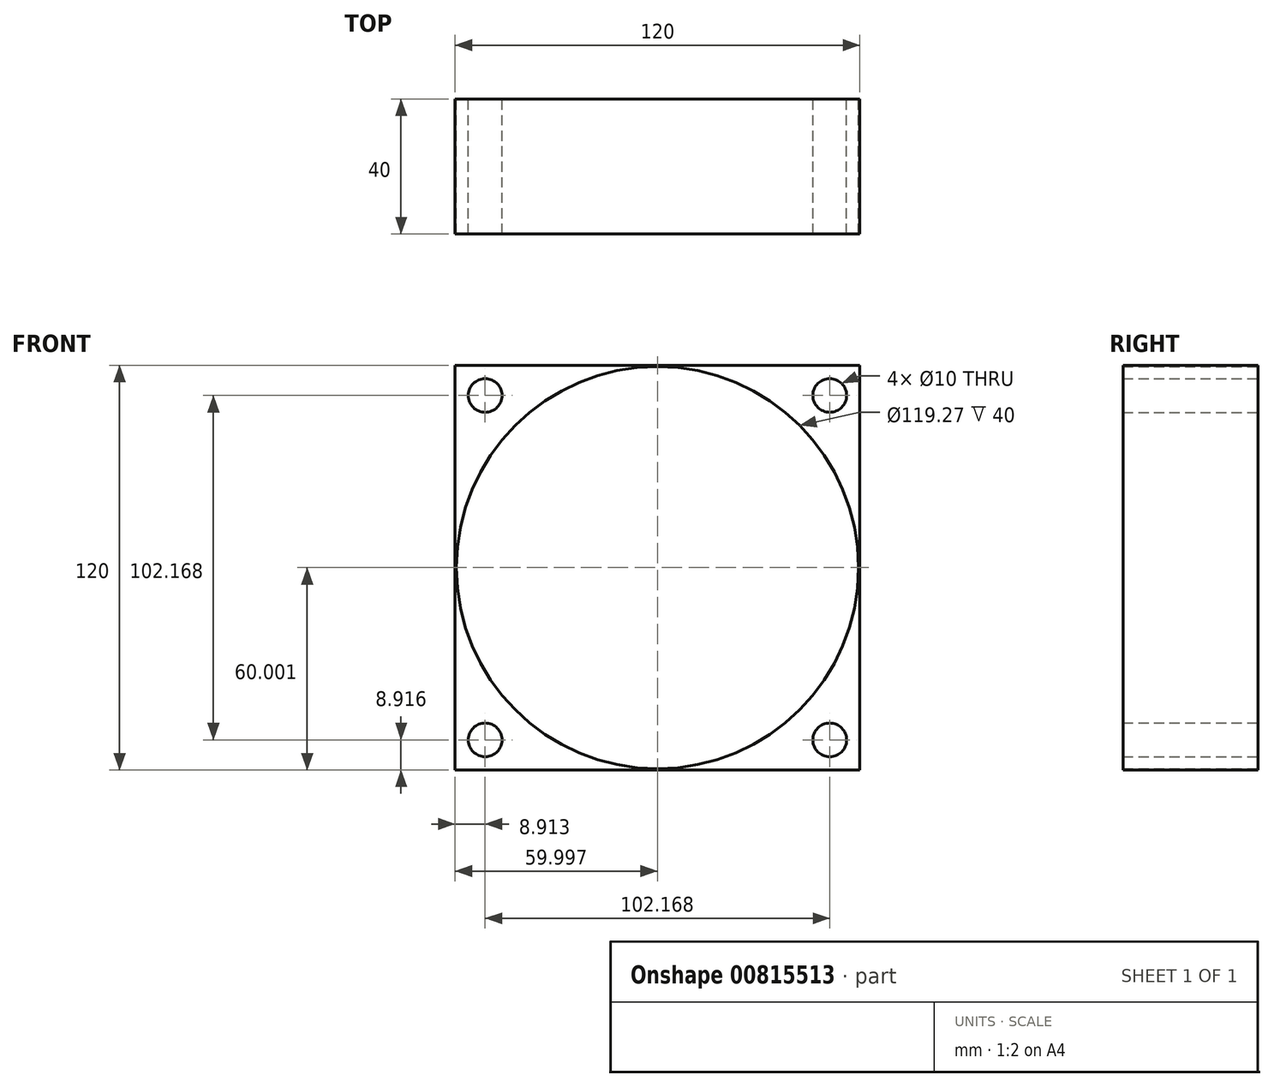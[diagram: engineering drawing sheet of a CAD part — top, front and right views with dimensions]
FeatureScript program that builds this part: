
annotation { "Feature Type Name" : "Feature", "Feature Type Description" : "" }
export const myFeature = defineFeature(function(context is Context, id is Id, definition is map)
    precondition{}
    {
        {
            var Q0;
            Q0=qCreatedBy(makeId("Front.planeOp"),FACE);
            var sketch = newSketch(context, id + "F0", { "sketchPlane" : qUnion([Q0])});
            skLineSegment(sketch, "E0.bottom", {"start": v(-45.86, 93.43) * mm, "end": v(74.14, 93.43) * mm});
            skLineSegment(sketch, "E0.top", {"start": v(-45.86, -26.57) * mm, "end": v(74.14, -26.57) * mm});
            skLineSegment(sketch, "E0.left", {"start": v(-45.86, 93.43) * mm, "end": v(-45.86, -26.57) * mm});
            skLineSegment(sketch, "E0.right", {"start": v(74.14, 93.43) * mm, "end": v(74.14, -26.57) * mm});
            skCircle(sketch, "E1", {"center": v(14.14, 33.43) * mm, "radius": 59.63 * mm});
            skCircle(sketch, "E2", {"center": v(-36.95, -17.65) * mm, "radius": 5 * mm});
            skCircle(sketch, "E3", {"center": v(65.22, -17.65) * mm, "radius": 5 * mm});
            skCircle(sketch, "E4", {"center": v(65.22, 84.51) * mm, "radius": 5 * mm});
            skCircle(sketch, "E5", {"center": v(-36.95, 84.51) * mm, "radius": 5 * mm});
            skPoint(sketch, "E6.end.orphan", {"position": v(-28.03, -8.74) * mm});
            skPoint(sketch, "E7.orphan", {"position": v(56.3, -8.74) * mm});
            skSolve(sketch);
        }
        {
            var Q0;
            Q0 = qSketchRegion(id + "F0", true);
            extrude(context, id + "F1", {"entities" : qUnion([Q0]), "depth" : 40 * mm, "offsetDistance" : 25 * mm});
        }
    });
